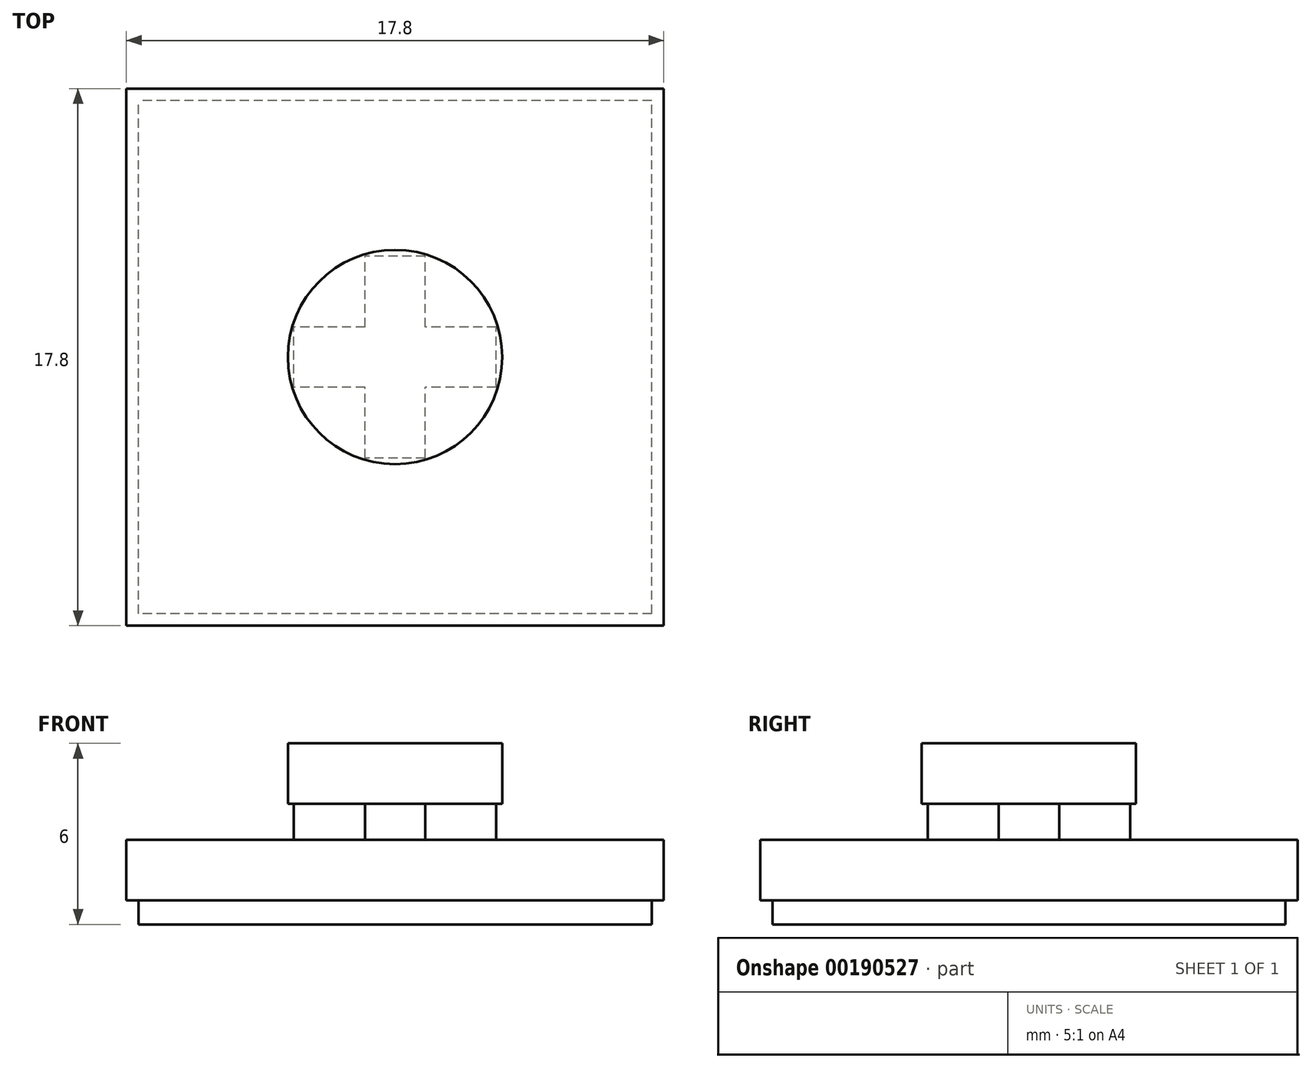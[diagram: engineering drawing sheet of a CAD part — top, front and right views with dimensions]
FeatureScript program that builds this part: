
annotation { "Feature Type Name" : "Feature", "Feature Type Description" : "" }
export const myFeature = defineFeature(function(context is Context, id is Id, definition is map)
    precondition{}
    {
        {
            assignVariable(context, id + "F0", {"name" : "A", "anyValue" : 6 * mm});
        }
        {
            var Q0;
            Q0=qCreatedBy(makeId("Top.planeOp"),FACE);
            var sketch = newSketch(context, id + "F1", { "sketchPlane" : qUnion([Q0])});
            skLineSegment(sketch, "E0.bottom", {"start": v(8.5, -8.5) * mm, "end": v(-8.5, -8.5) * mm});
            skLineSegment(sketch, "E0.top", {"start": v(8.5, 8.5) * mm, "end": v(-8.5, 8.5) * mm});
            skLineSegment(sketch, "E0.left", {"start": v(8.5, -8.5) * mm, "end": v(8.5, 8.5) * mm});
            skLineSegment(sketch, "E0.right", {"start": v(-8.5, -8.5) * mm, "end": v(-8.5, 8.5) * mm});
            skPoint(sketch, "E0.middle", {"position": v(0, 0) * mm});
            skSolve(sketch);
        }
        {
            var Q0;
            Q0=makeQuery(id+"F1.imprint","IMPRINT",FACE,{"disambiguationData":[TD([[makeQuery(id+"F1.imprint","IMPRINT",EDGE,{"derivedFrom":sQuery(id+"F1.wireOp",EDGE,"E0.bottom")}),-1.0]])]});
            extrude(context, id + "F2", {"entities" : qUnion([Q0]), "depth" : 0.8 * mm});
        }
        {
            var Q0;
            Q0=makeQuery(id+"F2.opExtrude","CAP_FACE",FACE,{"disambiguationData":[OSD([sQuery(id+"F1.wireOp",EDGE,"E0.bottom"),sQuery(id+"F1.wireOp",EDGE,"E0.top"),sQuery(id+"F1.wireOp",EDGE,"E0.left"),sQuery(id+"F1.wireOp",EDGE,"E0.right")])],"isStart":false});
            var sketch = newSketch(context, id + "F3", { "sketchPlane" : qUnion([Q0])});
            skLineSegment(sketch, "E1.bottom", {"start": v(8.9, -8.9) * mm, "end": v(-8.9, -8.9) * mm});
            skLineSegment(sketch, "E1.top", {"start": v(8.9, 8.9) * mm, "end": v(-8.9, 8.9) * mm});
            skLineSegment(sketch, "E1.left", {"start": v(8.9, -8.9) * mm, "end": v(8.9, 8.9) * mm});
            skLineSegment(sketch, "E1.right", {"start": v(-8.9, -8.9) * mm, "end": v(-8.9, 8.9) * mm});
            skPoint(sketch, "E1.middle", {"position": v(0, 0) * mm});
            skSolve(sketch);
        }
        {
            var Q0;
            Q0=makeQuery(id+"F3.imprint","IMPRINT",FACE,{"disambiguationData":[TD([[makeQuery(id+"F3.imprint","IMPRINT",EDGE,{"derivedFrom":makeQuery(id+"F2.opExtrude","CAP_EDGE",EDGE,{"disambiguationData":[OSD([sQuery(id+"F1.wireOp",EDGE,"E0.bottom")])],"isStart":false})}),-1.0]])]});
            var Q1;
            Q1=makeQuery(id+"F3.imprint","IMPRINT",FACE,{"disambiguationData":[TD([[makeQuery(id+"F3.imprint","IMPRINT",EDGE,{"derivedFrom":sQuery(id+"F3.wireOp",EDGE,"E1.bottom")}),-1.0]])]});
            extrude(context, id + "F4", {"entities" : qUnion([Q0, Q1]), "depth" : 2 * mm});
        }
        {
            var Q0;
            Q0=makeQuery(id+"F4.opExtrude","CAP_FACE",FACE,{"disambiguationData":[OSD([sQuery(id+"F3.wireOp",EDGE,"E1.bottom"),sQuery(id+"F3.wireOp",EDGE,"E1.top"),sQuery(id+"F3.wireOp",EDGE,"E1.left"),sQuery(id+"F3.wireOp",EDGE,"E1.right")])],"isStart":false});
            var sketch = newSketch(context, id + "F5", { "sketchPlane" : qUnion([Q0])});
            skLineSegment(sketch, "E2.bottom", {"start": v(1, -3.35) * mm, "end": v(-1, -3.35) * mm});
            skLineSegment(sketch, "E2.top", {"start": v(1, 3.35) * mm, "end": v(-1, 3.35) * mm});
            skLineSegment(sketch, "E2.left", {"start": v(1, -3.35) * mm, "end": v(1, 3.35) * mm});
            skLineSegment(sketch, "E2.right", {"start": v(-1, -3.35) * mm, "end": v(-1, 3.35) * mm});
            skPoint(sketch, "E2.middle", {"position": v(0, 0) * mm});
            skLineSegment(sketch, "E3.bottom", {"start": v(3.35, -1) * mm, "end": v(-3.35, -1) * mm});
            skLineSegment(sketch, "E3.top", {"start": v(3.35, 1) * mm, "end": v(-3.35, 1) * mm});
            skLineSegment(sketch, "E3.left", {"start": v(3.35, -1) * mm, "end": v(3.35, 1) * mm});
            skLineSegment(sketch, "E3.right", {"start": v(-3.35, -1) * mm, "end": v(-3.35, 1) * mm});
            skSolve(sketch);
        }
        {
            var Q0;
            {var subQ0=sQuery(id+"F5.wireOp",EDGE,"E2.top");Q0=makeQuery(id+"F5.imprint","IMPRINT",FACE,{"disambiguationData":[TD([[makeQuery(id+"F5.imprint","IMPRINT",EDGE,{"derivedFrom":subQ0}),1.0]])]});}
            var Q1;
            {var subQ0=sQuery(id+"F5.wireOp",EDGE,"E3.bottom");var subQ1=sQuery(id+"F5.wireOp",EDGE,"E2.left");var subQ2=makeQuery(id+"F5.imprint","INTERSECT",VERTEX,{"derivedFrom":[subQ1,subQ0]});Q1=makeQuery(id+"F5.imprint","IMPRINT",FACE,{"disambiguationData":[TD([[makeQuery(id+"F5.imprint","IMPRINT",EDGE,{"disambiguationData":[TD([[subQ2,-1.0]])],"derivedFrom":subQ1}),1.0]])]});}
            var Q2;
            {var subQ5=sQuery(id+"F5.wireOp",EDGE,"E3.left");Q2=makeQuery(id+"F5.imprint","IMPRINT",FACE,{"disambiguationData":[TD([[makeQuery(id+"F5.imprint","IMPRINT",EDGE,{"derivedFrom":subQ5}),1.0]])]});}
            var Q3;
            {var subQ5=sQuery(id+"F5.wireOp",EDGE,"E3.right");Q3=makeQuery(id+"F5.imprint","IMPRINT",FACE,{"disambiguationData":[TD([[makeQuery(id+"F5.imprint","IMPRINT",EDGE,{"derivedFrom":subQ5}),-1.0]])]});}
            var Q4;
            {var subQ0=sQuery(id+"F5.wireOp",EDGE,"E2.bottom");Q4=makeQuery(id+"F5.imprint","IMPRINT",FACE,{"disambiguationData":[TD([[makeQuery(id+"F5.imprint","IMPRINT",EDGE,{"derivedFrom":subQ0}),-1.0]])]});}
            extrude(context, id + "F6", {"entities" : qUnion([Q0, Q1, Q2, Q3, Q4]), "operationType" : NewBodyOperationType.ADD, "depth" : getVariable(context, 'A') - 4.8 * mm});
        }
        {
            var Q0;
            Q0=makeQuery(id+"F6.opExtrude","CAP_FACE",FACE,{"disambiguationData":[OSD([sQuery(id+"F5.wireOp",EDGE,"E2.bottom"),sQuery(id+"F5.wireOp",EDGE,"E2.top"),sQuery(id+"F5.wireOp",EDGE,"E2.left"),sQuery(id+"F5.wireOp",EDGE,"E2.right"),sQuery(id+"F5.wireOp",EDGE,"E3.bottom"),sQuery(id+"F5.wireOp",EDGE,"E3.top"),sQuery(id+"F5.wireOp",EDGE,"E3.left"),sQuery(id+"F5.wireOp",EDGE,"E3.right")])],"isStart":false});
            var sketch = newSketch(context, id + "F7", { "sketchPlane" : qUnion([Q0])});
            skCircle(sketch, "E4", {"center": v(0, 0) * mm, "radius": 3.55 * mm});
            skSolve(sketch);
        }
        {
            var Q0;
            {var subQ4=sQuery(id+"F5.wireOp",EDGE,"E2.bottom");Q0=makeQuery(id+"F7.imprint","IMPRINT",FACE,{"disambiguationData":[TD([[makeQuery(id+"F7.imprint","IMPRINT",EDGE,{"derivedFrom":makeQuery(id+"F6.opExtrude","CAP_EDGE",EDGE,{"disambiguationData":[OSD([subQ4])],"isStart":false})}),-1.0]])]});}
            var Q1;
            Q1=makeQuery(id+"F7.imprint","IMPRINT",FACE,{"disambiguationData":[TD([[makeQuery(id+"F7.imprint","IMPRINT",EDGE,{"derivedFrom":sQuery(id+"F7.wireOp",EDGE,"E4")}),1.0]])]});
            extrude(context, id + "F8", {"entities" : qUnion([Q0, Q1]), "operationType" : NewBodyOperationType.ADD, "depth" : 2 * mm});
        }
    });
